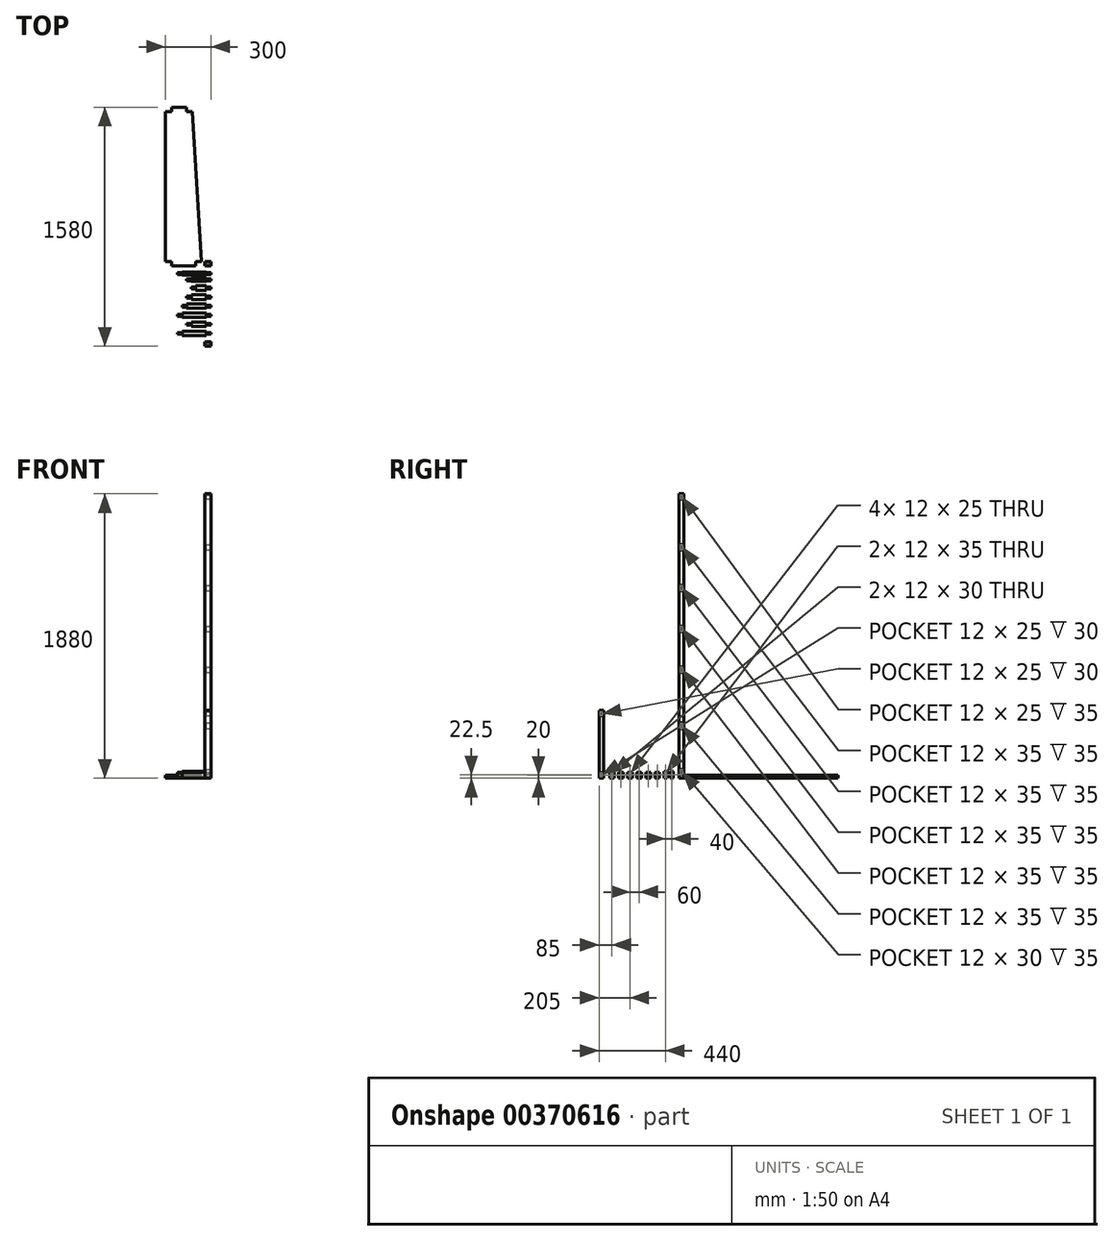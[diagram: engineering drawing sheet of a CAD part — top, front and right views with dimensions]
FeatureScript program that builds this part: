
annotation { "Feature Type Name" : "Feature", "Feature Type Description" : "" }
export const myFeature = defineFeature(function(context is Context, id is Id, definition is map)
    precondition{}
    {
        {
            var Q0;
            Q0=qCreatedBy(makeId("Right.planeOp"),FACE);
            var sketch = newSketch(context, id + "F0", { "sketchPlane" : qUnion([Q0])});
            skLineSegment(sketch, "E0", {"start": v(0, 0) * mm, "end": v(0, 1880) * mm});
            skLineSegment(sketch, "E1.bottom", {"start": v(0, 1880) * mm, "end": v(30, 1880) * mm});
            skLineSegment(sketch, "E1.top", {"start": v(0, 0) * mm, "end": v(30, 0) * mm});
            skLineSegment(sketch, "E1.right", {"start": v(30, 1880) * mm, "end": v(30, 0) * mm});
            skLineSegment(sketch, "E2.bottom", {"start": v(9, 57) * mm, "end": v(21, 57) * mm});
            skLineSegment(sketch, "E2.top", {"start": v(9, 27) * mm, "end": v(21, 27) * mm});
            skLineSegment(sketch, "E2.left", {"start": v(9, 57) * mm, "end": v(9, 27) * mm});
            skLineSegment(sketch, "E2.right", {"start": v(21, 57) * mm, "end": v(21, 27) * mm});
            skLineSegment(sketch, "E3.0.1.0", {"start": v(21, 365) * mm, "end": v(21, 330) * mm});
            skLineSegment(sketch, "E3.0.1.1", {"start": v(9, 365) * mm, "end": v(9, 330) * mm});
            skLineSegment(sketch, "E3.0.1.2", {"start": v(9, 365) * mm, "end": v(21, 365) * mm});
            skLineSegment(sketch, "E3.0.1.3", {"start": v(9, 330) * mm, "end": v(21, 330) * mm});
            skLineSegment(sketch, "E3.0.2.0", {"start": v(21, 735) * mm, "end": v(21, 700) * mm});
            skLineSegment(sketch, "E3.0.2.1", {"start": v(9, 735) * mm, "end": v(9, 700) * mm});
            skLineSegment(sketch, "E3.0.2.2", {"start": v(9, 735) * mm, "end": v(21, 735) * mm});
            skLineSegment(sketch, "E3.0.2.3", {"start": v(9, 700) * mm, "end": v(21, 700) * mm});
            skLineSegment(sketch, "E3.direction2", {"start": v(9, 27) * mm, "end": v(9, 1880) * mm, "construction": true});
            skLineSegment(sketch, "E4.bottom", {"start": v(9, 1870) * mm, "end": v(21, 1870) * mm});
            skLineSegment(sketch, "E4.top", {"start": v(9, 1845) * mm, "end": v(21, 1845) * mm});
            skLineSegment(sketch, "E4.left", {"start": v(9, 1870) * mm, "end": v(9, 1845) * mm});
            skLineSegment(sketch, "E4.right", {"start": v(21, 1870) * mm, "end": v(21, 1845) * mm});
            skLineSegment(sketch, "E5.0.1.0", {"start": v(9, 970) * mm, "end": v(21, 970) * mm});
            skLineSegment(sketch, "E5.0.1.1", {"start": v(9, 1005) * mm, "end": v(21, 1005) * mm});
            skLineSegment(sketch, "E5.0.1.2", {"start": v(9, 1005) * mm, "end": v(9, 970) * mm});
            skLineSegment(sketch, "E5.0.1.3", {"start": v(21, 1005) * mm, "end": v(21, 970) * mm});
            skLineSegment(sketch, "E5.0.2.0", {"start": v(9, 1240) * mm, "end": v(21, 1240) * mm});
            skLineSegment(sketch, "E5.0.2.1", {"start": v(9, 1275) * mm, "end": v(21, 1275) * mm});
            skLineSegment(sketch, "E5.0.2.2", {"start": v(9, 1275) * mm, "end": v(9, 1240) * mm});
            skLineSegment(sketch, "E5.0.2.3", {"start": v(21, 1275) * mm, "end": v(21, 1240) * mm});
            skLineSegment(sketch, "E5.0.3.0", {"start": v(9, 1510) * mm, "end": v(21, 1510) * mm});
            skLineSegment(sketch, "E5.0.3.1", {"start": v(9, 1545) * mm, "end": v(21, 1545) * mm});
            skLineSegment(sketch, "E5.0.3.2", {"start": v(9, 1545) * mm, "end": v(9, 1510) * mm});
            skLineSegment(sketch, "E5.0.3.3", {"start": v(21, 1545) * mm, "end": v(21, 1510) * mm});
            skLineSegment(sketch, "E5.direction1", {"start": v(9, 700) * mm, "end": v(34, 700) * mm, "construction": true});
            skLineSegment(sketch, "E5.direction2", {"start": v(9, 700) * mm, "end": v(9, 970) * mm, "construction": true});
            skSolve(sketch);
        }
        {
            var Q0;
            Q0=qCreatedBy(makeId("Right.planeOp"),FACE);
            var sketch = newSketch(context, id + "F1", { "sketchPlane" : qUnion([Q0])});
            skLineSegment(sketch, "E6.bottom", {"start": v(-40, 0) * mm, "end": v(-60, 0) * mm});
            skLineSegment(sketch, "E6.top", {"start": v(-40, 45) * mm, "end": v(-60, 45) * mm});
            skLineSegment(sketch, "E6.left", {"start": v(-40, 0) * mm, "end": v(-40, 45) * mm});
            skLineSegment(sketch, "E6.right", {"start": v(-60, 0) * mm, "end": v(-60, 45) * mm});
            skLineSegment(sketch, "E7.bottom", {"start": v(-56, 40) * mm, "end": v(-44, 40) * mm});
            skLineSegment(sketch, "E7.top", {"start": v(-56, 5) * mm, "end": v(-44, 5) * mm});
            skLineSegment(sketch, "E7.left", {"start": v(-56, 40) * mm, "end": v(-56, 5) * mm});
            skLineSegment(sketch, "E7.right", {"start": v(-44, 40) * mm, "end": v(-44, 5) * mm});
            skLineSegment(sketch, "E8.1.0.0", {"start": v(-84, 40) * mm, "end": v(-84, 5) * mm});
            skLineSegment(sketch, "E8.1.0.1", {"start": v(-80, 0) * mm, "end": v(-100, 0) * mm});
            skLineSegment(sketch, "E8.1.0.2", {"start": v(-80, 45) * mm, "end": v(-100, 45) * mm});
            skLineSegment(sketch, "E8.1.0.3", {"start": v(-80, 0) * mm, "end": v(-80, 45) * mm});
            skLineSegment(sketch, "E8.1.0.4", {"start": v(-100, 0) * mm, "end": v(-100, 45) * mm});
            skLineSegment(sketch, "E8.1.0.5", {"start": v(-96, 40) * mm, "end": v(-96, 5) * mm});
            skLineSegment(sketch, "E8.1.0.6", {"start": v(-96, 40) * mm, "end": v(-84, 40) * mm});
            skLineSegment(sketch, "E8.1.0.7", {"start": v(-96, 5) * mm, "end": v(-84, 5) * mm});
            skLineSegment(sketch, "E8.direction1", {"start": v(-60, 0) * mm, "end": v(-100, 0) * mm, "construction": true});
            skSolve(sketch);
        }
        {
            var Q0;
            Q0=makeQuery(id+"F1.imprint","IMPRINT",FACE,{"disambiguationData":[TD([[makeQuery(id+"F1.imprint","IMPRINT",EDGE,{"derivedFrom":sQuery(id+"F1.wireOp",EDGE,"E7.bottom")}),-1.0]])]});
            extrude(context, id + "F2", {"entities" : qUnion([Q0]), "oppositeDirection" : true, "depth" : 220 * mm});
        }
        {
            var Q0;
            Q0=makeQuery(id+"F1.imprint","IMPRINT",FACE,{"disambiguationData":[TD([[makeQuery(id+"F1.imprint","IMPRINT",EDGE,{"derivedFrom":sQuery(id+"F1.wireOp",EDGE,"E6.bottom")}),-1.0]])]});
            extrude(context, id + "F3", {"entities" : qUnion([Q0]), "operationType" : NewBodyOperationType.ADD, "oppositeDirection" : true, "depth" : 190 * mm, "hasSecondDirection" : true, "secondDirectionOppositeDirection" : true, "secondDirectionDepth" : 30 * mm});
        }
        {
            var Q0;
            Q0=makeQuery(id+"F1.imprint","IMPRINT",FACE,{"disambiguationData":[TD([[makeQuery(id+"F1.imprint","IMPRINT",EDGE,{"derivedFrom":sQuery(id+"F1.wireOp",EDGE,"E8.1.0.0")}),-1.0]])]});
            extrude(context, id + "F4", {"entities" : qUnion([Q0]), "oppositeDirection" : true, "depth" : 160 * mm});
        }
        {
            var Q0;
            Q0=makeQuery(id+"F1.imprint","IMPRINT",FACE,{"disambiguationData":[TD([[makeQuery(id+"F1.imprint","IMPRINT",EDGE,{"derivedFrom":sQuery(id+"F1.wireOp",EDGE,"E8.1.0.0")}),1.0]])]});
            extrude(context, id + "F5", {"entities" : qUnion([Q0]), "operationType" : NewBodyOperationType.ADD, "oppositeDirection" : true, "depth" : 130 * mm, "hasSecondDirection" : true, "secondDirectionOppositeDirection" : true, "secondDirectionDepth" : 30 * mm});
        }
        {
            var Q0;
            Q0=qCreatedBy(makeId("Top.planeOp"),FACE);
            var sketch = newSketch(context, id + "F6", { "sketchPlane" : qUnion([Q0])});
            skLineSegment(sketch, "E9", {"start": v(-102, 0) * mm, "end": v(-260, 0) * mm});
            skLineSegment(sketch, "E10", {"start": v(-260, 0) * mm, "end": v(-260, 30) * mm});
            skLineSegment(sketch, "E11", {"start": v(-260, 30) * mm, "end": v(-300, 30) * mm});
            skLineSegment(sketch, "E12", {"start": v(-300, 30) * mm, "end": v(-300, 1020) * mm});
            skLineSegment(sketch, "E13", {"start": v(-300, 1020) * mm, "end": v(-260, 1020) * mm});
            skLineSegment(sketch, "E14", {"start": v(-260, 1020) * mm, "end": v(-260, 1050) * mm});
            skLineSegment(sketch, "E15", {"start": v(-260, 1050) * mm, "end": v(-162, 1050) * mm});
            skLineSegment(sketch, "E16", {"start": v(-162, 1050) * mm, "end": v(-162, 1020) * mm});
            skLineSegment(sketch, "E17", {"start": v(-162, 1020) * mm, "end": v(-122, 1020) * mm});
            skLineSegment(sketch, "E18", {"start": v(-122, 1020) * mm, "end": v(-62, 30) * mm});
            skLineSegment(sketch, "E19", {"start": v(-62, 30) * mm, "end": v(-102, 30) * mm});
            skLineSegment(sketch, "E20", {"start": v(-102, 30) * mm, "end": v(-102, 0) * mm});
            skSolve(sketch);
        }
        {
            var Q0;
            Q0=makeQuery(id+"F6.imprint","IMPRINT",FACE,{"disambiguationData":[TD([[makeQuery(id+"F6.imprint","IMPRINT",EDGE,{"derivedFrom":sQuery(id+"F6.wireOp",EDGE,"E9")}),-1.0]])]});
            extrude(context, id + "F7", {"entities" : qUnion([Q0]), "depth" : 20 * mm});
        }
        {
            var Q0;
            Q0=makeQuery(id+"F7.opExtrude","CAP_EDGE",EDGE,{"disambiguationData":[OSD([sQuery(id+"F6.wireOp",EDGE,"E18")])],"isStart":false});
            var Q1;
            Q1=makeQuery(id+"F7.opExtrude","CAP_EDGE",EDGE,{"disambiguationData":[OSD([sQuery(id+"F6.wireOp",EDGE,"E18")])],"isStart":true});
            fillet(context, id + "F8", {"entities" : qUnion([Q0, Q1]), "radius" : 2 * mm, "allowEdgeOverflow" : false});
        }
        {
            var Q0;
            Q0=makeQuery(id+"F0.imprint","IMPRINT",FACE,{"disambiguationData":[TD([[makeQuery(id+"F0.imprint","IMPRINT",EDGE,{"derivedFrom":sQuery(id+"F0.wireOp",EDGE,"E0")}),-1.0]])]});
            var Q1;
            Q1=makeQuery(id+"F0.imprint","IMPRINT",FACE,{"disambiguationData":[TD([[makeQuery(id+"F0.imprint","IMPRINT",EDGE,{"derivedFrom":sQuery(id+"F0.wireOp",EDGE,"E5.0.3.0")}),1.0]])]});
            var Q2;
            Q2=makeQuery(id+"F0.imprint","IMPRINT",FACE,{"disambiguationData":[TD([[makeQuery(id+"F0.imprint","IMPRINT",EDGE,{"derivedFrom":sQuery(id+"F0.wireOp",EDGE,"E5.0.2.0")}),1.0]])]});
            var Q3;
            Q3=makeQuery(id+"F0.imprint","IMPRINT",FACE,{"disambiguationData":[TD([[makeQuery(id+"F0.imprint","IMPRINT",EDGE,{"derivedFrom":sQuery(id+"F0.wireOp",EDGE,"E5.0.1.0")}),1.0]])]});
            var Q4;
            Q4=makeQuery(id+"F0.imprint","IMPRINT",FACE,{"disambiguationData":[TD([[makeQuery(id+"F0.imprint","IMPRINT",EDGE,{"derivedFrom":sQuery(id+"F0.wireOp",EDGE,"E3.0.2.0")}),-1.0]])]});
            var Q5;
            Q5=makeQuery(id+"F0.imprint","IMPRINT",FACE,{"disambiguationData":[TD([[makeQuery(id+"F0.imprint","IMPRINT",EDGE,{"derivedFrom":sQuery(id+"F0.wireOp",EDGE,"E3.0.1.0")}),-1.0]])]});
            var Q6;
            Q6=makeQuery(id+"F0.imprint","IMPRINT",FACE,{"disambiguationData":[TD([[makeQuery(id+"F0.imprint","IMPRINT",EDGE,{"derivedFrom":sQuery(id+"F0.wireOp",EDGE,"E2.bottom")}),-1.0]])]});
            var Q7;
            Q7=makeQuery(id+"F0.imprint","IMPRINT",FACE,{"disambiguationData":[TD([[makeQuery(id+"F0.imprint","IMPRINT",EDGE,{"derivedFrom":sQuery(id+"F0.wireOp",EDGE,"E4.bottom")}),-1.0]])]});
            extrude(context, id + "F9", {"entities" : qUnion([Q0, Q1, Q2, Q3, Q4, Q5, Q6, Q7]), "oppositeDirection" : true, "depth" : 40 * mm});
        }
        {
            var Q0;
            Q0=makeQuery(id+"F0.imprint","IMPRINT",FACE,{"disambiguationData":[TD([[makeQuery(id+"F0.imprint","IMPRINT",EDGE,{"derivedFrom":sQuery(id+"F0.wireOp",EDGE,"E2.bottom")}),-1.0]])]});
            var Q1;
            Q1=makeQuery(id+"F0.imprint","IMPRINT",FACE,{"disambiguationData":[TD([[makeQuery(id+"F0.imprint","IMPRINT",EDGE,{"derivedFrom":sQuery(id+"F0.wireOp",EDGE,"E3.0.1.0")}),-1.0]])]});
            var Q2;
            Q2=makeQuery(id+"F0.imprint","IMPRINT",FACE,{"disambiguationData":[TD([[makeQuery(id+"F0.imprint","IMPRINT",EDGE,{"derivedFrom":sQuery(id+"F0.wireOp",EDGE,"E3.0.2.0")}),-1.0]])]});
            var Q3;
            Q3=makeQuery(id+"F0.imprint","IMPRINT",FACE,{"disambiguationData":[TD([[makeQuery(id+"F0.imprint","IMPRINT",EDGE,{"derivedFrom":sQuery(id+"F0.wireOp",EDGE,"E5.0.1.0")}),1.0]])]});
            var Q4;
            Q4=makeQuery(id+"F0.imprint","IMPRINT",FACE,{"disambiguationData":[TD([[makeQuery(id+"F0.imprint","IMPRINT",EDGE,{"derivedFrom":sQuery(id+"F0.wireOp",EDGE,"E5.0.2.0")}),1.0]])]});
            var Q5;
            Q5=makeQuery(id+"F0.imprint","IMPRINT",FACE,{"disambiguationData":[TD([[makeQuery(id+"F0.imprint","IMPRINT",EDGE,{"derivedFrom":sQuery(id+"F0.wireOp",EDGE,"E5.0.3.0")}),1.0]])]});
            var Q6;
            Q6=makeQuery(id+"F0.imprint","IMPRINT",FACE,{"disambiguationData":[TD([[makeQuery(id+"F0.imprint","IMPRINT",EDGE,{"derivedFrom":sQuery(id+"F0.wireOp",EDGE,"E4.bottom")}),-1.0]])]});
            extrude(context, id + "F10", {"entities" : qUnion([Q0, Q1, Q2, Q3, Q4, Q5, Q6]), "operationType" : NewBodyOperationType.REMOVE, "oppositeDirection" : true, "depth" : 35 * mm});
        }
        {
            var Q0;
            Q0=qCreatedBy(makeId("Right.planeOp"),FACE);
            var sketch = newSketch(context, id + "F11", { "sketchPlane" : qUnion([Q0])});
            skLineSegment(sketch, "E21.bottom", {"start": v(-130, 0) * mm, "end": v(-160, 0) * mm});
            skLineSegment(sketch, "E21.top", {"start": v(-130, 40) * mm, "end": v(-160, 40) * mm});
            skLineSegment(sketch, "E21.left", {"start": v(-130, 0) * mm, "end": v(-130, 40) * mm});
            skLineSegment(sketch, "E21.right", {"start": v(-160, 0) * mm, "end": v(-160, 40) * mm});
            skLineSegment(sketch, "E22.bottom", {"start": v(-139, 10) * mm, "end": v(-151, 10) * mm});
            skLineSegment(sketch, "E22.top", {"start": v(-139, 35) * mm, "end": v(-151, 35) * mm});
            skLineSegment(sketch, "E22.left", {"start": v(-139, 10) * mm, "end": v(-139, 35) * mm});
            skLineSegment(sketch, "E22.right", {"start": v(-151, 10) * mm, "end": v(-151, 35) * mm});
            skLineSegment(sketch, "E23.1.0.0", {"start": v(-199, 10) * mm, "end": v(-199, 35) * mm});
            skLineSegment(sketch, "E23.1.0.1", {"start": v(-211, 10) * mm, "end": v(-211, 35) * mm});
            skLineSegment(sketch, "E23.1.0.2", {"start": v(-199, 35) * mm, "end": v(-211, 35) * mm});
            skLineSegment(sketch, "E23.1.0.3", {"start": v(-199, 10) * mm, "end": v(-211, 10) * mm});
            skLineSegment(sketch, "E23.1.0.4", {"start": v(-220, 0) * mm, "end": v(-220, 40) * mm});
            skLineSegment(sketch, "E23.1.0.5", {"start": v(-190, 0) * mm, "end": v(-190, 40) * mm});
            skLineSegment(sketch, "E23.1.0.6", {"start": v(-190, 40) * mm, "end": v(-220, 40) * mm});
            skLineSegment(sketch, "E23.1.0.7", {"start": v(-190, 0) * mm, "end": v(-220, 0) * mm});
            skLineSegment(sketch, "E23.2.0.0", {"start": v(-259, 10) * mm, "end": v(-259, 35) * mm});
            skLineSegment(sketch, "E23.2.0.1", {"start": v(-271, 10) * mm, "end": v(-271, 35) * mm});
            skLineSegment(sketch, "E23.2.0.2", {"start": v(-259, 35) * mm, "end": v(-271, 35) * mm});
            skLineSegment(sketch, "E23.2.0.3", {"start": v(-259, 10) * mm, "end": v(-271, 10) * mm});
            skLineSegment(sketch, "E23.2.0.4", {"start": v(-280, 0) * mm, "end": v(-280, 40) * mm});
            skLineSegment(sketch, "E23.2.0.5", {"start": v(-250, 0) * mm, "end": v(-250, 40) * mm});
            skLineSegment(sketch, "E23.2.0.6", {"start": v(-250, 40) * mm, "end": v(-280, 40) * mm});
            skLineSegment(sketch, "E23.2.0.7", {"start": v(-250, 0) * mm, "end": v(-280, 0) * mm});
            skLineSegment(sketch, "E23.3.0.0", {"start": v(-319, 10) * mm, "end": v(-319, 35) * mm});
            skLineSegment(sketch, "E23.3.0.1", {"start": v(-331, 10) * mm, "end": v(-331, 35) * mm});
            skLineSegment(sketch, "E23.3.0.2", {"start": v(-319, 35) * mm, "end": v(-331, 35) * mm});
            skLineSegment(sketch, "E23.3.0.3", {"start": v(-319, 10) * mm, "end": v(-331, 10) * mm});
            skLineSegment(sketch, "E23.3.0.4", {"start": v(-340, 0) * mm, "end": v(-340, 40) * mm});
            skLineSegment(sketch, "E23.3.0.5", {"start": v(-310, 0) * mm, "end": v(-310, 40) * mm});
            skLineSegment(sketch, "E23.3.0.6", {"start": v(-310, 40) * mm, "end": v(-340, 40) * mm});
            skLineSegment(sketch, "E23.3.0.7", {"start": v(-310, 0) * mm, "end": v(-340, 0) * mm});
            skLineSegment(sketch, "E23.4.0.4", {"start": v(-400, 0) * mm, "end": v(-400, 40) * mm});
            skLineSegment(sketch, "E23.4.0.5", {"start": v(-370, 0) * mm, "end": v(-370, 40) * mm});
            skLineSegment(sketch, "E23.4.0.6", {"start": v(-370, 40) * mm, "end": v(-400, 40) * mm});
            skLineSegment(sketch, "E23.4.0.7", {"start": v(-370, 0) * mm, "end": v(-400, 0) * mm});
            skLineSegment(sketch, "E23.5.0.4", {"start": v(-460, 0) * mm, "end": v(-460, 40) * mm});
            skLineSegment(sketch, "E23.5.0.5", {"start": v(-430, 0) * mm, "end": v(-430, 40) * mm});
            skLineSegment(sketch, "E23.5.0.6", {"start": v(-430, 40) * mm, "end": v(-460, 40) * mm});
            skLineSegment(sketch, "E23.5.0.7", {"start": v(-430, 0) * mm, "end": v(-460, 0) * mm});
            skLineSegment(sketch, "E23.direction1", {"start": v(-160, 0) * mm, "end": v(-220, 0) * mm, "construction": true});
            skLineSegment(sketch, "E24.bottom", {"start": v(-379, 5) * mm, "end": v(-391, 5) * mm});
            skLineSegment(sketch, "E24.top", {"start": v(-379, 35) * mm, "end": v(-391, 35) * mm});
            skLineSegment(sketch, "E24.left", {"start": v(-379, 5) * mm, "end": v(-379, 35) * mm});
            skLineSegment(sketch, "E24.right", {"start": v(-391, 5) * mm, "end": v(-391, 35) * mm});
            skLineSegment(sketch, "E25.1.0.0", {"start": v(-439, 5) * mm, "end": v(-439, 35) * mm});
            skLineSegment(sketch, "E25.1.0.1", {"start": v(-451, 5) * mm, "end": v(-451, 35) * mm});
            skLineSegment(sketch, "E25.1.0.2", {"start": v(-439, 5) * mm, "end": v(-451, 5) * mm});
            skLineSegment(sketch, "E25.1.0.3", {"start": v(-439, 35) * mm, "end": v(-451, 35) * mm});
            skLineSegment(sketch, "E25.direction1", {"start": v(-391, 5) * mm, "end": v(-451, 5) * mm, "construction": true});
            skSolve(sketch);
        }
        {
            var Q0;
            Q0=makeQuery(id+"F11.imprint","IMPRINT",FACE,{"disambiguationData":[TD([[makeQuery(id+"F11.imprint","IMPRINT",EDGE,{"derivedFrom":sQuery(id+"F11.wireOp",EDGE,"E22.bottom")}),-1.0]])]});
            extrude(context, id + "F12", {"entities" : qUnion([Q0]), "oppositeDirection" : true, "depth" : 130 * mm});
        }
        {
            var Q0;
            Q0=makeQuery(id+"F11.imprint","IMPRINT",FACE,{"disambiguationData":[TD([[makeQuery(id+"F11.imprint","IMPRINT",EDGE,{"derivedFrom":sQuery(id+"F11.wireOp",EDGE,"E21.bottom")}),-1.0]])]});
            extrude(context, id + "F13", {"entities" : qUnion([Q0]), "operationType" : NewBodyOperationType.ADD, "oppositeDirection" : true, "depth" : 100 * mm, "hasSecondDirection" : true, "secondDirectionOppositeDirection" : true, "secondDirectionDepth" : 30 * mm});
        }
        {
            var Q0;
            Q0=makeQuery(id+"F11.imprint","IMPRINT",FACE,{"disambiguationData":[TD([[makeQuery(id+"F11.imprint","IMPRINT",EDGE,{"derivedFrom":sQuery(id+"F11.wireOp",EDGE,"E23.1.0.0")}),1.0]])]});
            extrude(context, id + "F14", {"entities" : qUnion([Q0]), "oppositeDirection" : true, "depth" : 160 * mm});
        }
        {
            var Q0;
            Q0=makeQuery(id+"F11.imprint","IMPRINT",FACE,{"disambiguationData":[TD([[makeQuery(id+"F11.imprint","IMPRINT",EDGE,{"derivedFrom":sQuery(id+"F11.wireOp",EDGE,"E23.1.0.0")}),-1.0]])]});
            extrude(context, id + "F15", {"entities" : qUnion([Q0]), "operationType" : NewBodyOperationType.ADD, "oppositeDirection" : true, "depth" : 130 * mm, "hasSecondDirection" : true, "secondDirectionOppositeDirection" : true, "secondDirectionDepth" : 30 * mm});
        }
        {
            var Q0;
            Q0=makeQuery(id+"F11.imprint","IMPRINT",FACE,{"disambiguationData":[TD([[makeQuery(id+"F11.imprint","IMPRINT",EDGE,{"derivedFrom":sQuery(id+"F11.wireOp",EDGE,"E23.2.0.0")}),1.0]])]});
            extrude(context, id + "F16", {"entities" : qUnion([Q0]), "oppositeDirection" : true, "depth" : 190 * mm});
        }
        {
            var Q0;
            Q0=makeQuery(id+"F11.imprint","IMPRINT",FACE,{"disambiguationData":[TD([[makeQuery(id+"F11.imprint","IMPRINT",EDGE,{"derivedFrom":sQuery(id+"F11.wireOp",EDGE,"E23.2.0.0")}),-1.0]])]});
            extrude(context, id + "F17", {"entities" : qUnion([Q0]), "operationType" : NewBodyOperationType.ADD, "oppositeDirection" : true, "depth" : 160 * mm, "hasSecondDirection" : true, "secondDirectionOppositeDirection" : true, "secondDirectionDepth" : 30 * mm});
        }
        {
            var Q0;
            Q0=makeQuery(id+"F11.imprint","IMPRINT",FACE,{"disambiguationData":[TD([[makeQuery(id+"F11.imprint","IMPRINT",EDGE,{"derivedFrom":sQuery(id+"F11.wireOp",EDGE,"E23.3.0.0")}),1.0]])]});
            extrude(context, id + "F18", {"entities" : qUnion([Q0]), "oppositeDirection" : true, "depth" : 220 * mm});
        }
        {
            var Q0;
            Q0=makeQuery(id+"F11.imprint","IMPRINT",FACE,{"disambiguationData":[TD([[makeQuery(id+"F11.imprint","IMPRINT",EDGE,{"derivedFrom":sQuery(id+"F11.wireOp",EDGE,"E23.3.0.0")}),-1.0]])]});
            extrude(context, id + "F19", {"entities" : qUnion([Q0]), "operationType" : NewBodyOperationType.ADD, "oppositeDirection" : true, "depth" : 190 * mm, "hasSecondDirection" : true, "secondDirectionOppositeDirection" : true, "secondDirectionDepth" : 30 * mm});
        }
        {
            var Q0;
            Q0=makeQuery(id+"F11.imprint","IMPRINT",FACE,{"disambiguationData":[TD([[makeQuery(id+"F11.imprint","IMPRINT",EDGE,{"derivedFrom":sQuery(id+"F11.wireOp",EDGE,"E24.bottom")}),-1.0]])]});
            extrude(context, id + "F20", {"entities" : qUnion([Q0]), "oppositeDirection" : true, "depth" : 160 * mm});
        }
        {
            var Q0;
            Q0=makeQuery(id+"F11.imprint","IMPRINT",FACE,{"disambiguationData":[TD([[makeQuery(id+"F11.imprint","IMPRINT",EDGE,{"derivedFrom":sQuery(id+"F11.wireOp",EDGE,"E23.4.0.4")}),-1.0]])]});
            extrude(context, id + "F21", {"entities" : qUnion([Q0]), "operationType" : NewBodyOperationType.ADD, "oppositeDirection" : true, "depth" : 130 * mm, "hasSecondDirection" : true, "secondDirectionOppositeDirection" : true, "secondDirectionDepth" : 30 * mm});
        }
        {
            var Q0;
            Q0=makeQuery(id+"F11.imprint","IMPRINT",FACE,{"disambiguationData":[TD([[makeQuery(id+"F11.imprint","IMPRINT",EDGE,{"derivedFrom":sQuery(id+"F11.wireOp",EDGE,"E25.1.0.0")}),1.0]])]});
            extrude(context, id + "F22", {"entities" : qUnion([Q0]), "oppositeDirection" : true, "depth" : 220 * mm});
        }
        {
            var Q0;
            Q0=makeQuery(id+"F11.imprint","IMPRINT",FACE,{"disambiguationData":[TD([[makeQuery(id+"F11.imprint","IMPRINT",EDGE,{"derivedFrom":sQuery(id+"F11.wireOp",EDGE,"E23.5.0.4")}),-1.0]])]});
            extrude(context, id + "F23", {"entities" : qUnion([Q0]), "operationType" : NewBodyOperationType.ADD, "oppositeDirection" : true, "depth" : 190 * mm, "hasSecondDirection" : true, "secondDirectionOppositeDirection" : true, "secondDirectionDepth" : 30 * mm});
        }
        {
            var Q0;
            Q0=qCreatedBy(makeId("Right.planeOp"),FACE);
            var sketch = newSketch(context, id + "F24", { "sketchPlane" : qUnion([Q0])});
            skLineSegment(sketch, "E26.bottom", {"start": v(-500, 0) * mm, "end": v(-530, 0) * mm});
            skLineSegment(sketch, "E26.top", {"start": v(-500, 450) * mm, "end": v(-530, 450) * mm});
            skLineSegment(sketch, "E26.left", {"start": v(-500, 0) * mm, "end": v(-500, 450) * mm});
            skLineSegment(sketch, "E26.right", {"start": v(-530, 0) * mm, "end": v(-530, 450) * mm});
            skLineSegment(sketch, "E27.bottom", {"start": v(-509, 10) * mm, "end": v(-521, 10) * mm});
            skLineSegment(sketch, "E27.top", {"start": v(-509, 35) * mm, "end": v(-521, 35) * mm});
            skLineSegment(sketch, "E27.left", {"start": v(-509, 10) * mm, "end": v(-509, 35) * mm});
            skLineSegment(sketch, "E27.right", {"start": v(-521, 10) * mm, "end": v(-521, 35) * mm});
            skPoint(sketch, "E28.oppositeSnap0", {"position": v(-521, 22.5) * mm});
            skLineSegment(sketch, "E28.bottom", {"start": v(-509, 415) * mm, "end": v(-521, 415) * mm});
            skLineSegment(sketch, "E28.top", {"start": v(-509, 440) * mm, "end": v(-521, 440) * mm});
            skLineSegment(sketch, "E28.left", {"start": v(-509, 415) * mm, "end": v(-509, 440) * mm});
            skLineSegment(sketch, "E28.right", {"start": v(-521, 415) * mm, "end": v(-521, 440) * mm});
            skSolve(sketch);
        }
        {
            var Q0;
            Q0=makeQuery(id+"F24.imprint","IMPRINT",FACE,{"disambiguationData":[TD([[makeQuery(id+"F24.imprint","IMPRINT",EDGE,{"derivedFrom":sQuery(id+"F24.wireOp",EDGE,"E26.bottom")}),-1.0]])]});
            var Q1;
            Q1=makeQuery(id+"F24.imprint","IMPRINT",FACE,{"disambiguationData":[TD([[makeQuery(id+"F24.imprint","IMPRINT",EDGE,{"derivedFrom":sQuery(id+"F24.wireOp",EDGE,"E28.bottom")}),-1.0]])]});
            var Q2;
            Q2=makeQuery(id+"F24.imprint","IMPRINT",FACE,{"disambiguationData":[TD([[makeQuery(id+"F24.imprint","IMPRINT",EDGE,{"derivedFrom":sQuery(id+"F24.wireOp",EDGE,"E27.bottom")}),-1.0]])]});
            extrude(context, id + "F25", {"entities" : qUnion([Q0, Q1, Q2]), "oppositeDirection" : true, "depth" : 40 * mm});
        }
        {
            var Q0;
            Q0=makeQuery(id+"F24.imprint","IMPRINT",FACE,{"disambiguationData":[TD([[makeQuery(id+"F24.imprint","IMPRINT",EDGE,{"derivedFrom":sQuery(id+"F24.wireOp",EDGE,"E28.bottom")}),-1.0]])]});
            var Q1;
            Q1=makeQuery(id+"F24.imprint","IMPRINT",FACE,{"disambiguationData":[TD([[makeQuery(id+"F24.imprint","IMPRINT",EDGE,{"derivedFrom":sQuery(id+"F24.wireOp",EDGE,"E27.bottom")}),-1.0]])]});
            extrude(context, id + "F26", {"entities" : qUnion([Q0, Q1]), "operationType" : NewBodyOperationType.REMOVE, "oppositeDirection" : true, "depth" : 30 * mm});
        }
    });
